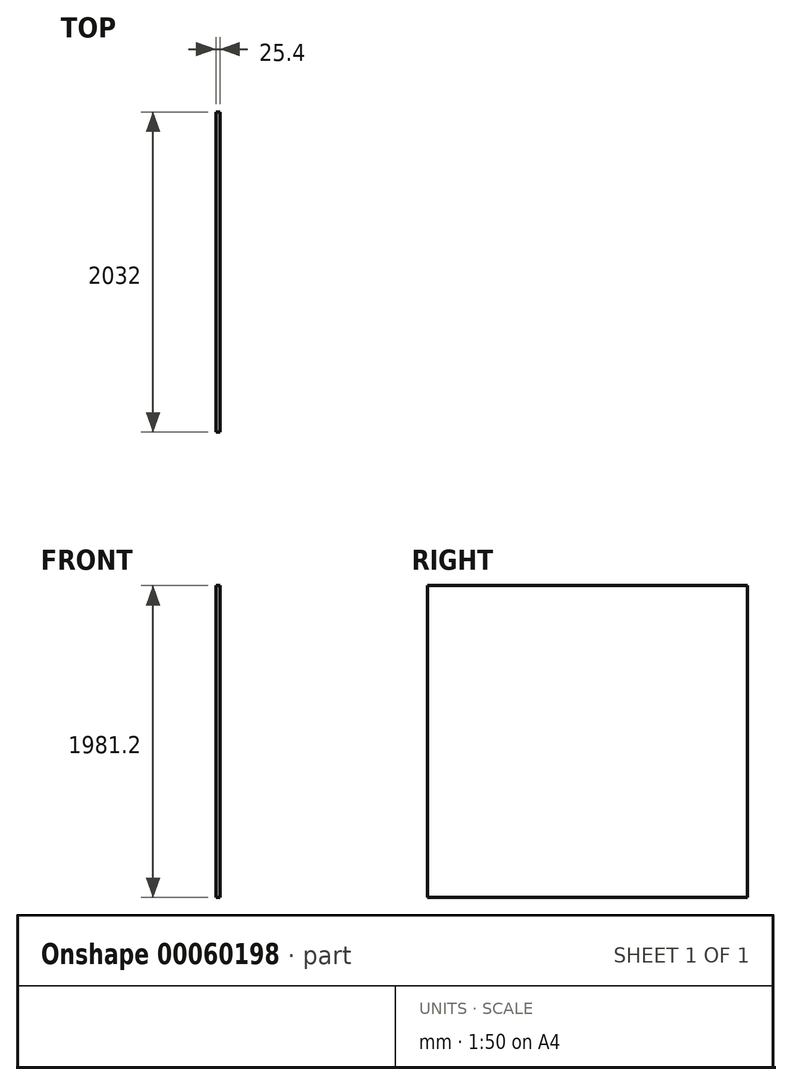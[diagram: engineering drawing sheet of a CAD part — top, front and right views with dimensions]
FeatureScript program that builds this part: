
annotation { "Feature Type Name" : "Feature", "Feature Type Description" : "" }
export const myFeature = defineFeature(function(context is Context, id is Id, definition is map)
    precondition{}
    {
        {
            var Q0;
            Q0=qCreatedBy(makeId("Right.planeOp"),FACE);
            var sketch = newSketch(context, id + "F0", { "sketchPlane" : qUnion([Q0])});
            skLineSegment(sketch, "E0.rect.bottom", {"start": v(1016, 990.6) * mm, "end": v(-1016, 990.6) * mm});
            skLineSegment(sketch, "E0.rect.top", {"start": v(1016, -990.6) * mm, "end": v(-1016, -990.6) * mm});
            skLineSegment(sketch, "E0.rect.left", {"start": v(1016, 990.6) * mm, "end": v(1016, -990.6) * mm});
            skLineSegment(sketch, "E0.rect.right", {"start": v(-1016, 990.6) * mm, "end": v(-1016, -990.6) * mm});
            skPoint(sketch, "E0.rect.middle", {"position": v(0, 0) * mm});
            skSolve(sketch);
        }
        {
            var Q0;
            Q0=makeQuery(id+"F0.imprint","IMPRINT",FACE,{"disambiguationData":[TD([[makeQuery(id+"F0.imprint","IMPRINT",EDGE,{"derivedFrom":sQuery(id+"F0.wireOp",EDGE,"E0.rect.bottom")}),1.0]])]});
            extrude(context, id + "F1", {"entities" : qUnion([Q0]), "depth" : 25.4 * mm});
        }
    });
